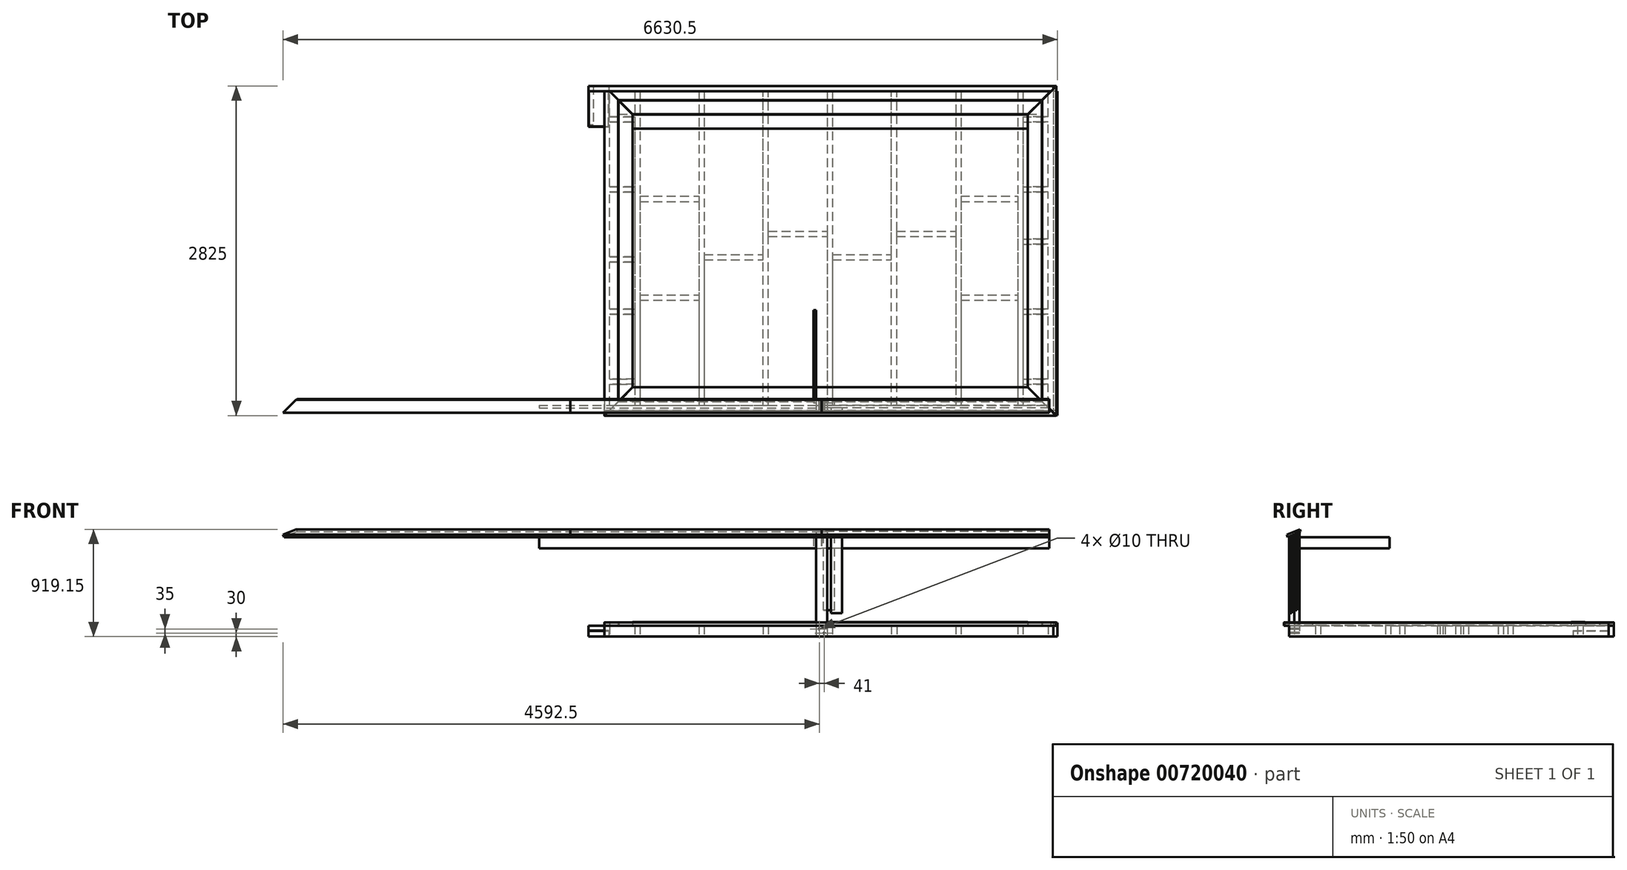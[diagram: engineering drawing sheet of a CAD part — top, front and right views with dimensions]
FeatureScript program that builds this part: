
annotation { "Feature Type Name" : "Feature", "Feature Type Description" : "" }
export const myFeature = defineFeature(function(context is Context, id is Id, definition is map)
    precondition{}
    {
        {
            var Q0;
            Q0=qCreatedBy(makeId("Top.planeOp"),FACE);
            var sketch = newSketch(context, id + "F0", { "sketchPlane" : qUnion([Q0])});
            skLineSegment(sketch, "E0.bottom", {"start": v(0, 0) * mm, "end": v(3980, 0) * mm});
            skLineSegment(sketch, "E0.top", {"start": v(0, -45) * mm, "end": v(3980, -45) * mm});
            skLineSegment(sketch, "E0.left", {"start": v(0, 0) * mm, "end": v(0, -45) * mm});
            skLineSegment(sketch, "E0.right", {"start": v(3980, 0) * mm, "end": v(3980, -45) * mm});
            skLineSegment(sketch, "E1.bottom", {"start": v(135, -2737) * mm, "end": v(3980, -2737) * mm});
            skLineSegment(sketch, "E1.top", {"start": v(135, -2782) * mm, "end": v(3980, -2782) * mm});
            skLineSegment(sketch, "E1.left", {"start": v(135, -2737) * mm, "end": v(135, -2782) * mm});
            skLineSegment(sketch, "E1.right", {"start": v(3980, -2737) * mm, "end": v(3980, -2782) * mm});
            skSolve(sketch);
        }
        {
            var Q0;
            Q0=makeQuery(id+"F0.imprint","IMPRINT",FACE,{"disambiguationData":[TD([[makeQuery(id+"F0.imprint","IMPRINT",EDGE,{"derivedFrom":sQuery(id+"F0.wireOp",EDGE,"E0.bottom")}),-1.0]])]});
            var Q1;
            Q1=makeQuery(id+"F0.imprint","IMPRINT",FACE,{"disambiguationData":[TD([[makeQuery(id+"F0.imprint","IMPRINT",EDGE,{"derivedFrom":sQuery(id+"F0.wireOp",EDGE,"E1.bottom")}),-1.0]])]});
            extrude(context, id + "F1", {"entities" : qUnion([Q0, Q1]), "depth" : 94 * mm, "offsetDistance" : 25 * mm});
        }
        {
            var Q0;
            Q0=qCreatedBy(makeId("Top.planeOp"),FACE);
            var sketch = newSketch(context, id + "F2", { "sketchPlane" : qUnion([Q0])});
            skLineSegment(sketch, "E2.bottom", {"start": v(945, -45) * mm, "end": v(990, -45) * mm});
            skLineSegment(sketch, "E2.top", {"start": v(945, -2737) * mm, "end": v(990, -2737) * mm});
            skLineSegment(sketch, "E2.left", {"start": v(945, -45) * mm, "end": v(945, -2737) * mm});
            skLineSegment(sketch, "E2.right", {"start": v(990, -45) * mm, "end": v(990, -2737) * mm});
            skLineSegment(sketch, "E3.bottom", {"start": v(1495, -2737) * mm, "end": v(1540, -2737) * mm});
            skLineSegment(sketch, "E3.top", {"start": v(1495, -45) * mm, "end": v(1540, -45) * mm});
            skLineSegment(sketch, "E3.left", {"start": v(1495, -2737) * mm, "end": v(1495, -45) * mm});
            skLineSegment(sketch, "E3.right", {"start": v(1540, -2737) * mm, "end": v(1540, -45) * mm});
            skLineSegment(sketch, "E4.bottom", {"start": v(2045, -45) * mm, "end": v(2090, -45) * mm});
            skLineSegment(sketch, "E4.top", {"start": v(2045, -2737) * mm, "end": v(2090, -2737) * mm});
            skLineSegment(sketch, "E4.left", {"start": v(2045, -45) * mm, "end": v(2045, -2737) * mm});
            skLineSegment(sketch, "E4.right", {"start": v(2090, -45) * mm, "end": v(2090, -2737) * mm});
            skLineSegment(sketch, "E5.bottom", {"start": v(2595, -2737) * mm, "end": v(2640, -2737) * mm});
            skLineSegment(sketch, "E5.top", {"start": v(2595, -45) * mm, "end": v(2640, -45) * mm});
            skLineSegment(sketch, "E5.left", {"start": v(2595, -2737) * mm, "end": v(2595, -45) * mm});
            skLineSegment(sketch, "E5.right", {"start": v(2640, -2737) * mm, "end": v(2640, -45) * mm});
            skLineSegment(sketch, "E6.bottom", {"start": v(3145, -45) * mm, "end": v(3190, -45) * mm});
            skLineSegment(sketch, "E6.top", {"start": v(3145, -2737) * mm, "end": v(3190, -2737) * mm});
            skLineSegment(sketch, "E6.left", {"start": v(3145, -45) * mm, "end": v(3145, -2737) * mm});
            skLineSegment(sketch, "E6.right", {"start": v(3190, -45) * mm, "end": v(3190, -2737) * mm});
            skLineSegment(sketch, "E7.bottom", {"start": v(3935, -2737) * mm, "end": v(3980, -2737) * mm});
            skLineSegment(sketch, "E7.top", {"start": v(3935, -45) * mm, "end": v(3980, -45) * mm});
            skLineSegment(sketch, "E7.left", {"start": v(3935, -2737) * mm, "end": v(3935, -45) * mm});
            skLineSegment(sketch, "E7.right", {"start": v(3980, -2737) * mm, "end": v(3980, -45) * mm});
            skLineSegment(sketch, "E8.bottom", {"start": v(395, -45) * mm, "end": v(440, -45) * mm});
            skLineSegment(sketch, "E8.top", {"start": v(395, -2737) * mm, "end": v(440, -2737) * mm});
            skLineSegment(sketch, "E8.left", {"start": v(395, -45) * mm, "end": v(395, -2737) * mm});
            skLineSegment(sketch, "E8.right", {"start": v(440, -45) * mm, "end": v(440, -2737) * mm});
            skLineSegment(sketch, "E9.bottom", {"start": v(3720, -45) * mm, "end": v(3675, -45) * mm});
            skLineSegment(sketch, "E9.top", {"start": v(3720, -2737) * mm, "end": v(3675, -2737) * mm});
            skLineSegment(sketch, "E9.left", {"start": v(3720, -45) * mm, "end": v(3720, -2737) * mm});
            skLineSegment(sketch, "E9.right", {"start": v(3675, -45) * mm, "end": v(3675, -2737) * mm});
            skLineSegment(sketch, "E10.0", {"start": v(0, -45) * mm, "end": v(3980, -45) * mm});
            skPoint(sketch, "E11.0", {"position": v(135, -2737) * mm});
            skLineSegment(sketch, "E12.bottom", {"start": v(135, -2737) * mm, "end": v(180, -2737) * mm});
            skLineSegment(sketch, "E12.top", {"start": v(135, -45) * mm, "end": v(180, -45) * mm});
            skLineSegment(sketch, "E12.left", {"start": v(135, -2737) * mm, "end": v(135, -45) * mm});
            skLineSegment(sketch, "E12.right", {"start": v(180, -2737) * mm, "end": v(180, -45) * mm});
            skSolve(sketch);
        }
        {
            var Q0;
            Q0=makeQuery(id+"F2.imprint","IMPRINT",FACE,{"disambiguationData":[TD([[makeQuery(id+"F2.imprint","IMPRINT",EDGE,{"derivedFrom":sQuery(id+"F2.wireOp",EDGE,"E12.bottom")}),1.0]])]});
            var Q1;
            Q1=makeQuery(id+"F2.imprint","IMPRINT",FACE,{"disambiguationData":[TD([[makeQuery(id+"F2.imprint","IMPRINT",EDGE,{"derivedFrom":sQuery(id+"F2.wireOp",EDGE,"E8.top")}),1.0]])]});
            var Q2;
            Q2=makeQuery(id+"F2.imprint","IMPRINT",FACE,{"disambiguationData":[TD([[makeQuery(id+"F2.imprint","IMPRINT",EDGE,{"derivedFrom":sQuery(id+"F2.wireOp",EDGE,"E2.top")}),1.0]])]});
            var Q3;
            Q3=makeQuery(id+"F2.imprint","IMPRINT",FACE,{"disambiguationData":[TD([[makeQuery(id+"F2.imprint","IMPRINT",EDGE,{"derivedFrom":sQuery(id+"F2.wireOp",EDGE,"E3.bottom")}),1.0]])]});
            var Q4;
            Q4=makeQuery(id+"F2.imprint","IMPRINT",FACE,{"disambiguationData":[TD([[makeQuery(id+"F2.imprint","IMPRINT",EDGE,{"derivedFrom":sQuery(id+"F2.wireOp",EDGE,"E4.top")}),1.0]])]});
            var Q5;
            Q5=makeQuery(id+"F2.imprint","IMPRINT",FACE,{"disambiguationData":[TD([[makeQuery(id+"F2.imprint","IMPRINT",EDGE,{"derivedFrom":sQuery(id+"F2.wireOp",EDGE,"E5.bottom")}),1.0]])]});
            var Q6;
            Q6=makeQuery(id+"F2.imprint","IMPRINT",FACE,{"disambiguationData":[TD([[makeQuery(id+"F2.imprint","IMPRINT",EDGE,{"derivedFrom":sQuery(id+"F2.wireOp",EDGE,"E6.top")}),1.0]])]});
            var Q7;
            Q7=makeQuery(id+"F2.imprint","IMPRINT",FACE,{"disambiguationData":[TD([[makeQuery(id+"F2.imprint","IMPRINT",EDGE,{"derivedFrom":sQuery(id+"F2.wireOp",EDGE,"E9.top")}),-1.0]])]});
            var Q8;
            Q8=makeQuery(id+"F2.imprint","IMPRINT",FACE,{"disambiguationData":[TD([[makeQuery(id+"F2.imprint","IMPRINT",EDGE,{"derivedFrom":sQuery(id+"F2.wireOp",EDGE,"E7.bottom")}),1.0]])]});
            extrude(context, id + "F3", {"entities" : qUnion([Q0, Q1, Q2, Q3, Q4, Q5, Q6, Q7, Q8]), "operationType" : NewBodyOperationType.ADD, "depth" : 95.5 * mm, "offsetDistance" : 25 * mm});
        }
        {
            var Q0;
            Q0=makeQuery(id+"F1.opExtrude","CAP_FACE",FACE,{"disambiguationData":[OSD([sQuery(id+"F0.wireOp",EDGE,"E0.bottom"),sQuery(id+"F0.wireOp",EDGE,"E0.top"),sQuery(id+"F0.wireOp",EDGE,"E0.left"),sQuery(id+"F0.wireOp",EDGE,"E0.right")])],"isStart":false});
            var sketch = newSketch(context, id + "F4", { "sketchPlane" : qUnion([Q0])});
            skLineSegment(sketch, "E13.bottom", {"start": v(135.7, 0) * mm, "end": v(4004.3, 0) * mm});
            skLineSegment(sketch, "E14.0", {"start": v(135.7, 0) * mm, "end": v(255.7, -120) * mm});
            skLineSegment(sketch, "E15.trimOffspring", {"start": v(255.7, -120) * mm, "end": v(3884.3, -120) * mm});
            skPoint(sketch, "E16.0", {"position": v(135, -2782) * mm});
            skLineSegment(sketch, "E17.left", {"start": v(135, -2824.3) * mm, "end": v(135, -0.7) * mm});
            skLineSegment(sketch, "E17.right", {"start": v(255, -2704.3) * mm, "end": v(255, -120.7) * mm});
            skPoint(sketch, "E18.0", {"position": v(0, 0) * mm});
            skLineSegment(sketch, "E19", {"start": v(135, -0.7) * mm, "end": v(255, -120.7) * mm});
            skLineSegment(sketch, "E20", {"start": v(135, -2824.3) * mm, "end": v(255, -2704.3) * mm});
            skLineSegment(sketch, "E21.bottom", {"start": v(135.7, -2825) * mm, "end": v(4004.3, -2825) * mm});
            skLineSegment(sketch, "E21.top", {"start": v(255.7, -2705) * mm, "end": v(3884.3, -2705) * mm});
            skPoint(sketch, "E22.0", {"position": v(3980, -2782) * mm});
            skLineSegment(sketch, "E23", {"start": v(3884.3, -2705) * mm, "end": v(4004.3, -2825) * mm});
            skLineSegment(sketch, "E24", {"start": v(255.7, -2705) * mm, "end": v(135.7, -2825) * mm});
            skLineSegment(sketch, "E25.left", {"start": v(4005, -0.7) * mm, "end": v(4005, -2824.3) * mm});
            skLineSegment(sketch, "E25.right", {"start": v(3885, -120.7) * mm, "end": v(3885, -2704.3) * mm});
            skLineSegment(sketch, "E26", {"start": v(4005, -2824.3) * mm, "end": v(3885, -2704.3) * mm});
            skLineSegment(sketch, "E27", {"start": v(4005, -0.7) * mm, "end": v(3885, -120.7) * mm});
            skLineSegment(sketch, "E28", {"start": v(3884.3, -120) * mm, "end": v(4004.3, 0) * mm});
            skPoint(sketch, "E29.0", {"position": v(3980, 0) * mm});
            skLineSegment(sketch, "E30", {"start": v(4004.3, 0) * mm, "end": v(4005, -0.7) * mm, "construction": true});
            skLineSegment(sketch, "E31", {"start": v(135.7, 0) * mm, "end": v(135, -0.7) * mm, "construction": true});
            skLineSegment(sketch, "E32", {"start": v(135.7, -2825) * mm, "end": v(135, -2824.3) * mm, "construction": true});
            skLineSegment(sketch, "E33", {"start": v(3881.3, -123) * mm, "end": v(3761.3, -243) * mm});
            skLineSegment(sketch, "E34", {"start": v(3761.3, -243) * mm, "end": v(378.7, -243) * mm});
            skLineSegment(sketch, "E35", {"start": v(378.7, -243) * mm, "end": v(258.7, -123) * mm});
            skLineSegment(sketch, "E36", {"start": v(258.7, -123) * mm, "end": v(3881.3, -123) * mm});
            skLineSegment(sketch, "E37", {"start": v(258, -123.7) * mm, "end": v(258, -2701.3) * mm});
            skLineSegment(sketch, "E38", {"start": v(258, -2701.3) * mm, "end": v(378, -2581.3) * mm});
            skLineSegment(sketch, "E39", {"start": v(378, -2581.3) * mm, "end": v(378, -243.7) * mm});
            skLineSegment(sketch, "E40", {"start": v(378, -243.7) * mm, "end": v(258, -123.7) * mm});
            skLineSegment(sketch, "E41", {"start": v(3762, -243.7) * mm, "end": v(3882, -123.7) * mm});
            skLineSegment(sketch, "E42", {"start": v(3882, -123.7) * mm, "end": v(3882, -2701.3) * mm});
            skLineSegment(sketch, "E43", {"start": v(3882, -2701.3) * mm, "end": v(3762, -2581.3) * mm});
            skLineSegment(sketch, "E44", {"start": v(3762, -2581.3) * mm, "end": v(3762, -243.7) * mm});
            skLineSegment(sketch, "E45", {"start": v(3761.3, -2582) * mm, "end": v(3881.3, -2702) * mm});
            skLineSegment(sketch, "E46", {"start": v(3881.3, -2702) * mm, "end": v(258.7, -2702) * mm});
            skLineSegment(sketch, "E47", {"start": v(258.7, -2702) * mm, "end": v(378.7, -2582) * mm});
            skLineSegment(sketch, "E48", {"start": v(378.7, -2582) * mm, "end": v(3761.3, -2582) * mm});
            skLineSegment(sketch, "E49", {"start": v(4005, -2824.3) * mm, "end": v(4004.3, -2825) * mm});
            skSolve(sketch);
        }
        {
            var Q0;
            {var subQ0=sQuery(id+"F4.wireOp",EDGE,"E15.trimOffspring");Q0=makeQuery(id+"F4.imprint","IMPRINT",FACE,{"disambiguationData":[TD([[makeQuery(id+"F4.imprint","IMPRINT",EDGE,{"derivedFrom":subQ0}),1.0]])]});}
            var Q1;
            {var subQ0=sQuery(id+"F4.wireOp",EDGE,"E13.bottom");Q1=makeQuery(id+"F4.imprint","IMPRINT",FACE,{"disambiguationData":[TD([[makeQuery(id+"F4.imprint","IMPRINT",EDGE,{"derivedFrom":subQ0}),-1.0]])]});}
            var Q2;
            {var subQ1=sQuery(id+"F4.wireOp",EDGE,"E17.right");Q2=makeQuery(id+"F4.imprint","IMPRINT",FACE,{"disambiguationData":[TD([[makeQuery(id+"F4.imprint","IMPRINT",EDGE,{"derivedFrom":subQ1}),1.0]])]});}
            var Q3;
            {var subQ0=sQuery(id+"F4.wireOp",EDGE,"E17.left");var subQ1=makeQuery(id+"F1.opExtrude","CAP_EDGE",EDGE,{"disambiguationData":[OSD([sQuery(id+"F0.wireOp",EDGE,"E0.top")])],"isStart":false});var subQ2=makeQuery(id+"F4.imprint","INTERSECT",VERTEX,{"derivedFrom":[subQ1,subQ0]});Q3=makeQuery(id+"F4.imprint","IMPRINT",FACE,{"disambiguationData":[TD([[makeQuery(id+"F4.imprint","IMPRINT",EDGE,{"disambiguationData":[TD([[subQ2,-1.0]])],"derivedFrom":subQ1}),1.0]])]});}
            var Q4;
            Q4=makeQuery(id+"F4.imprint","IMPRINT",FACE,{"disambiguationData":[TD([[makeQuery(id+"F4.imprint","IMPRINT",EDGE,{"derivedFrom":sQuery(id+"F4.wireOp",EDGE,"E21.top")}),-1.0]])]});
            var Q5;
            {var subQ1=sQuery(id+"F4.wireOp",EDGE,"E25.right");Q5=makeQuery(id+"F4.imprint","IMPRINT",FACE,{"disambiguationData":[TD([[makeQuery(id+"F4.imprint","IMPRINT",EDGE,{"derivedFrom":subQ1}),1.0]])]});}
            var Q6;
            Q6=makeQuery(id+"F4.imprint","IMPRINT",FACE,{"disambiguationData":[TD([[makeQuery(id+"F4.imprint","IMPRINT",EDGE,{"derivedFrom":sQuery(id+"F4.wireOp",EDGE,"E33")}),-1.0]])]});
            var Q7;
            Q7=makeQuery(id+"F4.imprint","IMPRINT",FACE,{"disambiguationData":[TD([[makeQuery(id+"F4.imprint","IMPRINT",EDGE,{"derivedFrom":sQuery(id+"F4.wireOp",EDGE,"E37")}),1.0]])]});
            var Q8;
            Q8=makeQuery(id+"F4.imprint","IMPRINT",FACE,{"disambiguationData":[TD([[makeQuery(id+"F4.imprint","IMPRINT",EDGE,{"derivedFrom":sQuery(id+"F4.wireOp",EDGE,"E41")}),-1.0]])]});
            var Q9;
            Q9=makeQuery(id+"F4.imprint","IMPRINT",FACE,{"disambiguationData":[TD([[makeQuery(id+"F4.imprint","IMPRINT",EDGE,{"derivedFrom":sQuery(id+"F4.wireOp",EDGE,"E45")}),-1.0]])]});
            var Q10;
            {var subQ3=sQuery(id+"F4.wireOp",EDGE,"E28");var subQ5=makeQuery(id+"F1.opExtrude","CAP_EDGE",EDGE,{"disambiguationData":[OSD([sQuery(id+"F0.wireOp",EDGE,"E0.top")])],"isStart":false});var subQ6=makeQuery(id+"F4.imprint","INTERSECT",VERTEX,{"derivedFrom":[subQ5,subQ3]});Q10=makeQuery(id+"F4.imprint","IMPRINT",FACE,{"disambiguationData":[TD([[makeQuery(id+"F4.imprint","IMPRINT",EDGE,{"disambiguationData":[TD([[subQ6,-1.0]])],"derivedFrom":subQ3}),1.0]])]});}
            var Q11;
            {var subQ0=sQuery(id+"F4.wireOp",EDGE,"E27");var subQ1=makeQuery(id+"F1.opExtrude","CAP_EDGE",EDGE,{"disambiguationData":[OSD([sQuery(id+"F0.wireOp",EDGE,"E0.right")])],"isStart":false});var subQ2=makeQuery(id+"F4.imprint","INTERSECT",VERTEX,{"derivedFrom":[subQ1,subQ0]});Q11=makeQuery(id+"F4.imprint","IMPRINT",FACE,{"disambiguationData":[TD([[makeQuery(id+"F4.imprint","IMPRINT",EDGE,{"disambiguationData":[TD([[subQ2,-1.0]])],"derivedFrom":subQ0}),1.0]])]});}
            extrude(context, id + "F5", {"entities" : qUnion([Q0, Q1, Q2, Q3, Q4, Q5, Q6, Q7, Q8, Q9, Q10, Q11]), "depth" : 28 * mm, "offsetDistance" : 25 * mm});
        }
        {
            var Q0;
            Q0=qCreatedBy(makeId("Top.planeOp"),FACE);
            var sketch = newSketch(context, id + "F6", { "sketchPlane" : qUnion([Q0])});
            skLineSegment(sketch, "E50.0", {"start": v(945, -45) * mm, "end": v(945, -2737) * mm});
            skLineSegment(sketch, "E51.bottom", {"start": v(440, -1792) * mm, "end": v(945, -1792) * mm});
            skLineSegment(sketch, "E51.top", {"start": v(440, -1837) * mm, "end": v(945, -1837) * mm});
            skLineSegment(sketch, "E51.left", {"start": v(440, -1792) * mm, "end": v(440, -1837) * mm});
            skLineSegment(sketch, "E51.right", {"start": v(945, -1792) * mm, "end": v(945, -1837) * mm});
            skLineSegment(sketch, "E52.0", {"start": v(990, -45) * mm, "end": v(990, -2737) * mm});
            skLineSegment(sketch, "E53.0", {"start": v(1495, -2737) * mm, "end": v(1495, -45) * mm});
            skLineSegment(sketch, "E54.bottom", {"start": v(990, -1445) * mm, "end": v(1495, -1445) * mm});
            skLineSegment(sketch, "E54.top", {"start": v(990, -1490) * mm, "end": v(1495, -1490) * mm});
            skLineSegment(sketch, "E54.left", {"start": v(990, -1445) * mm, "end": v(990, -1490) * mm});
            skLineSegment(sketch, "E54.right", {"start": v(1495, -1445) * mm, "end": v(1495, -1490) * mm});
            skLineSegment(sketch, "E55.0", {"start": v(1540, -2737) * mm, "end": v(1540, -45) * mm});
            skLineSegment(sketch, "E56.0", {"start": v(2045, -45) * mm, "end": v(2045, -2737) * mm});
            skLineSegment(sketch, "E57.0", {"start": v(2090, -45) * mm, "end": v(2090, -2737) * mm});
            skLineSegment(sketch, "E58.0", {"start": v(2595, -2737) * mm, "end": v(2595, -45) * mm});
            skLineSegment(sketch, "E59.0", {"start": v(2640, -2737) * mm, "end": v(2640, -45) * mm});
            skLineSegment(sketch, "E60.0", {"start": v(3145, -45) * mm, "end": v(3145, -2737) * mm});
            skLineSegment(sketch, "E61.0", {"start": v(3190, -45) * mm, "end": v(3190, -2737) * mm});
            skLineSegment(sketch, "E62.0", {"start": v(3935, -2737) * mm, "end": v(3935, -45) * mm});
            skLineSegment(sketch, "E63.bottom", {"start": v(1540, -1290) * mm, "end": v(2045, -1290) * mm});
            skLineSegment(sketch, "E63.top", {"start": v(1540, -1245) * mm, "end": v(2045, -1245) * mm});
            skLineSegment(sketch, "E63.left", {"start": v(1540, -1290) * mm, "end": v(1540, -1245) * mm});
            skLineSegment(sketch, "E63.right", {"start": v(2045, -1290) * mm, "end": v(2045, -1245) * mm});
            skLineSegment(sketch, "E64.bottom", {"start": v(2090, -1445) * mm, "end": v(2595, -1445) * mm});
            skLineSegment(sketch, "E64.top", {"start": v(2090, -1490) * mm, "end": v(2595, -1490) * mm});
            skLineSegment(sketch, "E64.left", {"start": v(2090, -1445) * mm, "end": v(2090, -1490) * mm});
            skLineSegment(sketch, "E64.right", {"start": v(2595, -1445) * mm, "end": v(2595, -1490) * mm});
            skLineSegment(sketch, "E65.bottom", {"start": v(2640, -1290) * mm, "end": v(3145, -1290) * mm});
            skLineSegment(sketch, "E65.top", {"start": v(2640, -1245) * mm, "end": v(3145, -1245) * mm});
            skLineSegment(sketch, "E65.left", {"start": v(2640, -1290) * mm, "end": v(2640, -1245) * mm});
            skLineSegment(sketch, "E65.right", {"start": v(3145, -1290) * mm, "end": v(3145, -1245) * mm});
            skLineSegment(sketch, "E66.bottom", {"start": v(3190, -945) * mm, "end": v(3675, -945) * mm});
            skLineSegment(sketch, "E66.top", {"start": v(3190, -990) * mm, "end": v(3675, -990) * mm});
            skLineSegment(sketch, "E66.left", {"start": v(3190, -945) * mm, "end": v(3190, -990) * mm});
            skLineSegment(sketch, "E66.right", {"start": v(3675, -945) * mm, "end": v(3675, -990) * mm});
            skLineSegment(sketch, "E67.bottom", {"start": v(3190, -1792) * mm, "end": v(3675, -1792) * mm});
            skLineSegment(sketch, "E67.top", {"start": v(3190, -1837) * mm, "end": v(3675, -1837) * mm});
            skLineSegment(sketch, "E67.left", {"start": v(3190, -1792) * mm, "end": v(3190, -1837) * mm});
            skLineSegment(sketch, "E67.right", {"start": v(3675, -1792) * mm, "end": v(3675, -1837) * mm});
            skLineSegment(sketch, "E68.0", {"start": v(440, -45) * mm, "end": v(440, -2737) * mm});
            skLineSegment(sketch, "E69.bottom", {"start": v(440, -990) * mm, "end": v(945, -990) * mm});
            skLineSegment(sketch, "E69.top", {"start": v(440, -945) * mm, "end": v(945, -945) * mm});
            skLineSegment(sketch, "E69.left", {"start": v(440, -990) * mm, "end": v(440, -945) * mm});
            skLineSegment(sketch, "E69.right", {"start": v(945, -990) * mm, "end": v(945, -945) * mm});
            skLineSegment(sketch, "E70.0", {"start": v(395, -45) * mm, "end": v(395, -2737) * mm});
            skLineSegment(sketch, "E71.0", {"start": v(180, -2737) * mm, "end": v(180, -45) * mm});
            skLineSegment(sketch, "E72.bottom", {"start": v(180, -310) * mm, "end": v(395, -310) * mm});
            skLineSegment(sketch, "E72.top", {"start": v(180, -265) * mm, "end": v(395, -265) * mm});
            skLineSegment(sketch, "E72.left", {"start": v(180, -310) * mm, "end": v(180, -265) * mm});
            skLineSegment(sketch, "E72.right", {"start": v(395, -310) * mm, "end": v(395, -265) * mm});
            skLineSegment(sketch, "E73.bottom", {"start": v(395, -2557) * mm, "end": v(180, -2557) * mm});
            skLineSegment(sketch, "E73.top", {"start": v(395, -2512) * mm, "end": v(180, -2512) * mm});
            skLineSegment(sketch, "E73.left", {"start": v(395, -2557) * mm, "end": v(395, -2512) * mm});
            skLineSegment(sketch, "E73.right", {"start": v(180, -2557) * mm, "end": v(180, -2512) * mm});
            skLineSegment(sketch, "E74.bottom", {"start": v(180, -1957) * mm, "end": v(395, -1957) * mm});
            skLineSegment(sketch, "E74.top", {"start": v(180, -1912) * mm, "end": v(395, -1912) * mm});
            skLineSegment(sketch, "E74.left", {"start": v(180, -1957) * mm, "end": v(180, -1912) * mm});
            skLineSegment(sketch, "E74.right", {"start": v(395, -1957) * mm, "end": v(395, -1912) * mm});
            skLineSegment(sketch, "E75.bottom", {"start": v(180, -1510) * mm, "end": v(395, -1510) * mm});
            skLineSegment(sketch, "E75.top", {"start": v(180, -1465) * mm, "end": v(395, -1465) * mm});
            skLineSegment(sketch, "E75.left", {"start": v(180, -1510) * mm, "end": v(180, -1465) * mm});
            skLineSegment(sketch, "E75.right", {"start": v(395, -1510) * mm, "end": v(395, -1465) * mm});
            skLineSegment(sketch, "E76.bottom", {"start": v(180, -910) * mm, "end": v(395, -910) * mm});
            skLineSegment(sketch, "E76.top", {"start": v(180, -865) * mm, "end": v(395, -865) * mm});
            skLineSegment(sketch, "E76.left", {"start": v(180, -910) * mm, "end": v(180, -865) * mm});
            skLineSegment(sketch, "E76.right", {"start": v(395, -910) * mm, "end": v(395, -865) * mm});
            skLineSegment(sketch, "E77.0", {"start": v(3720, -45) * mm, "end": v(3720, -2737) * mm});
            skLineSegment(sketch, "E78.bottom", {"start": v(3720, -2557) * mm, "end": v(3935, -2557) * mm});
            skLineSegment(sketch, "E78.top", {"start": v(3720, -2512) * mm, "end": v(3935, -2512) * mm});
            skLineSegment(sketch, "E78.left", {"start": v(3720, -2557) * mm, "end": v(3720, -2512) * mm});
            skLineSegment(sketch, "E78.right", {"start": v(3935, -2557) * mm, "end": v(3935, -2512) * mm});
            skLineSegment(sketch, "E79.bottom", {"start": v(3720, -1957) * mm, "end": v(3935, -1957) * mm});
            skLineSegment(sketch, "E79.top", {"start": v(3720, -1912) * mm, "end": v(3935, -1912) * mm});
            skLineSegment(sketch, "E79.left", {"start": v(3720, -1957) * mm, "end": v(3720, -1912) * mm});
            skLineSegment(sketch, "E79.right", {"start": v(3935, -1957) * mm, "end": v(3935, -1912) * mm});
            skLineSegment(sketch, "E80.bottom", {"start": v(3720, -1357) * mm, "end": v(3935, -1357) * mm});
            skLineSegment(sketch, "E80.top", {"start": v(3720, -1312) * mm, "end": v(3935, -1312) * mm});
            skLineSegment(sketch, "E80.left", {"start": v(3720, -1357) * mm, "end": v(3720, -1312) * mm});
            skLineSegment(sketch, "E80.right", {"start": v(3935, -1357) * mm, "end": v(3935, -1312) * mm});
            skLineSegment(sketch, "E81.bottom", {"start": v(3720, -265) * mm, "end": v(3935, -265) * mm});
            skLineSegment(sketch, "E81.top", {"start": v(3720, -310) * mm, "end": v(3935, -310) * mm});
            skLineSegment(sketch, "E81.left", {"start": v(3720, -265) * mm, "end": v(3720, -310) * mm});
            skLineSegment(sketch, "E81.right", {"start": v(3935, -265) * mm, "end": v(3935, -310) * mm});
            skLineSegment(sketch, "E82.bottom", {"start": v(3720, -910) * mm, "end": v(3935, -910) * mm});
            skLineSegment(sketch, "E82.top", {"start": v(3720, -865) * mm, "end": v(3935, -865) * mm});
            skLineSegment(sketch, "E82.left", {"start": v(3720, -910) * mm, "end": v(3720, -865) * mm});
            skLineSegment(sketch, "E82.right", {"start": v(3935, -910) * mm, "end": v(3935, -865) * mm});
            skSolve(sketch);
        }
        {
            var Q0;
            Q0=makeQuery(id+"F6.imprint","IMPRINT",FACE,{"disambiguationData":[TD([[makeQuery(id+"F6.imprint","IMPRINT",EDGE,{"derivedFrom":sQuery(id+"F6.wireOp",EDGE,"E72.bottom")}),1.0]])]});
            var Q1;
            Q1=makeQuery(id+"F6.imprint","IMPRINT",FACE,{"disambiguationData":[TD([[makeQuery(id+"F6.imprint","IMPRINT",EDGE,{"derivedFrom":sQuery(id+"F6.wireOp",EDGE,"E76.bottom")}),1.0]])]});
            var Q2;
            Q2=makeQuery(id+"F6.imprint","IMPRINT",FACE,{"disambiguationData":[TD([[makeQuery(id+"F6.imprint","IMPRINT",EDGE,{"derivedFrom":sQuery(id+"F6.wireOp",EDGE,"E75.bottom")}),1.0]])]});
            var Q3;
            Q3=makeQuery(id+"F6.imprint","IMPRINT",FACE,{"disambiguationData":[TD([[makeQuery(id+"F6.imprint","IMPRINT",EDGE,{"derivedFrom":sQuery(id+"F6.wireOp",EDGE,"E69.bottom")}),1.0]])]});
            var Q4;
            {var subQ0=sQuery(id+"F6.wireOp",EDGE,"E51.bottom");Q4=makeQuery(id+"F6.imprint","IMPRINT",FACE,{"disambiguationData":[TD([[makeQuery(id+"F6.imprint","IMPRINT",EDGE,{"derivedFrom":subQ0}),-1.0]])]});}
            var Q5;
            Q5=makeQuery(id+"F6.imprint","IMPRINT",FACE,{"disambiguationData":[TD([[makeQuery(id+"F6.imprint","IMPRINT",EDGE,{"derivedFrom":sQuery(id+"F6.wireOp",EDGE,"E74.bottom")}),1.0]])]});
            var Q6;
            Q6=makeQuery(id+"F6.imprint","IMPRINT",FACE,{"disambiguationData":[TD([[makeQuery(id+"F6.imprint","IMPRINT",EDGE,{"derivedFrom":sQuery(id+"F6.wireOp",EDGE,"E73.bottom")}),-1.0]])]});
            var Q7;
            Q7=makeQuery(id+"F6.imprint","IMPRINT",FACE,{"disambiguationData":[TD([[makeQuery(id+"F6.imprint","IMPRINT",EDGE,{"derivedFrom":sQuery(id+"F6.wireOp",EDGE,"E54.bottom")}),-1.0]])]});
            var Q8;
            Q8=makeQuery(id+"F6.imprint","IMPRINT",FACE,{"disambiguationData":[TD([[makeQuery(id+"F6.imprint","IMPRINT",EDGE,{"derivedFrom":sQuery(id+"F6.wireOp",EDGE,"E63.bottom")}),1.0]])]});
            var Q9;
            Q9=makeQuery(id+"F6.imprint","IMPRINT",FACE,{"disambiguationData":[TD([[makeQuery(id+"F6.imprint","IMPRINT",EDGE,{"derivedFrom":sQuery(id+"F6.wireOp",EDGE,"E64.bottom")}),-1.0]])]});
            var Q10;
            Q10=makeQuery(id+"F6.imprint","IMPRINT",FACE,{"disambiguationData":[TD([[makeQuery(id+"F6.imprint","IMPRINT",EDGE,{"derivedFrom":sQuery(id+"F6.wireOp",EDGE,"E65.bottom")}),1.0]])]});
            var Q11;
            Q11=makeQuery(id+"F6.imprint","IMPRINT",FACE,{"disambiguationData":[TD([[makeQuery(id+"F6.imprint","IMPRINT",EDGE,{"derivedFrom":sQuery(id+"F6.wireOp",EDGE,"E66.bottom")}),-1.0]])]});
            var Q12;
            Q12=makeQuery(id+"F6.imprint","IMPRINT",FACE,{"disambiguationData":[TD([[makeQuery(id+"F6.imprint","IMPRINT",EDGE,{"derivedFrom":sQuery(id+"F6.wireOp",EDGE,"E67.bottom")}),-1.0]])]});
            var Q13;
            Q13=makeQuery(id+"F6.imprint","IMPRINT",FACE,{"disambiguationData":[TD([[makeQuery(id+"F6.imprint","IMPRINT",EDGE,{"derivedFrom":sQuery(id+"F6.wireOp",EDGE,"E78.bottom")}),1.0]])]});
            var Q14;
            Q14=makeQuery(id+"F6.imprint","IMPRINT",FACE,{"disambiguationData":[TD([[makeQuery(id+"F6.imprint","IMPRINT",EDGE,{"derivedFrom":sQuery(id+"F6.wireOp",EDGE,"E79.bottom")}),1.0]])]});
            var Q15;
            Q15=makeQuery(id+"F6.imprint","IMPRINT",FACE,{"disambiguationData":[TD([[makeQuery(id+"F6.imprint","IMPRINT",EDGE,{"derivedFrom":sQuery(id+"F6.wireOp",EDGE,"E80.bottom")}),1.0]])]});
            var Q16;
            Q16=makeQuery(id+"F6.imprint","IMPRINT",FACE,{"disambiguationData":[TD([[makeQuery(id+"F6.imprint","IMPRINT",EDGE,{"derivedFrom":sQuery(id+"F6.wireOp",EDGE,"E82.bottom")}),1.0]])]});
            var Q17;
            Q17=makeQuery(id+"F6.imprint","IMPRINT",FACE,{"disambiguationData":[TD([[makeQuery(id+"F6.imprint","IMPRINT",EDGE,{"derivedFrom":sQuery(id+"F6.wireOp",EDGE,"E81.bottom")}),-1.0]])]});
            extrude(context, id + "F7", {"entities" : qUnion([Q0, Q1, Q2, Q3, Q4, Q5, Q6, Q7, Q8, Q9, Q10, Q11, Q12, Q13, Q14, Q15, Q16, Q17]), "operationType" : NewBodyOperationType.ADD, "depth" : 95 * mm, "offsetDistance" : 25 * mm});
        }
        {
            var Q0;
            Q0=qCreatedBy(makeId("Top.planeOp"),FACE);
            var sketch = newSketch(context, id + "F8", { "sketchPlane" : qUnion([Q0])});
            skPoint(sketch, "E83.0", {"position": v(2045, -2737) * mm});
            skLineSegment(sketch, "E84.bottom", {"start": v(2045, -2737) * mm, "end": v(1950, -2737) * mm});
            skLineSegment(sketch, "E84.top", {"start": v(2045, -2692) * mm, "end": v(1950, -2692) * mm});
            skLineSegment(sketch, "E84.left", {"start": v(2045, -2737) * mm, "end": v(2045, -2692) * mm});
            skLineSegment(sketch, "E84.right", {"start": v(1950, -2737) * mm, "end": v(1950, -2692) * mm});
            skSolve(sketch);
        }
        {
            var Q0;
            Q0=makeQuery(id+"F8.imprint","IMPRINT",FACE,{"disambiguationData":[TD([[makeQuery(id+"F8.imprint","IMPRINT",EDGE,{"derivedFrom":sQuery(id+"F8.wireOp",EDGE,"E84.bottom")}),-1.0]])]});
            extrude(context, id + "F9", {"entities" : qUnion([Q0]), "depth" : 895 * mm, "offsetDistance" : 25 * mm});
        }
        {
            var Q0;
            Q0=makeQuery(id+"F9.opExtrude","SWEPT_EDGE",EDGE,{"disambiguationData":[OSD([sQuery(id+"F8.wireOp",EDGE,"E84.bottom"),sQuery(id+"F8.wireOp",EDGE,"E84.right")])]});
            var Q1;
            Q1=makeQuery(id+"F9.opExtrude","SWEPT_EDGE",EDGE,{"disambiguationData":[OSD([sQuery(id+"F8.wireOp",EDGE,"E84.bottom"),sQuery(id+"F8.wireOp",EDGE,"E84.left")])]});
            var Q2;
            Q2=makeQuery(id+"F9.opExtrude","SWEPT_EDGE",EDGE,{"disambiguationData":[OSD([sQuery(id+"F8.wireOp",EDGE,"E84.top"),sQuery(id+"F8.wireOp",EDGE,"E84.left")])]});
            var Q3;
            Q3=makeQuery(id+"F9.opExtrude","SWEPT_EDGE",EDGE,{"disambiguationData":[OSD([sQuery(id+"F8.wireOp",EDGE,"E84.top"),sQuery(id+"F8.wireOp",EDGE,"E84.right")])]});
            fillet(context, id + "F10", {"entities" : qUnion([Q0, Q1, Q2, Q3]), "radius" : 2 * mm, "tangentPropagation" : true, "allowEdgeOverflow" : false});
        }
        {
            var Q0;
            Q0=makeQuery(id+"F9.opExtrude","CAP_FACE",FACE,{"disambiguationData":[OSD([sQuery(id+"F8.wireOp",EDGE,"E84.bottom"),sQuery(id+"F8.wireOp",EDGE,"E84.top"),sQuery(id+"F8.wireOp",EDGE,"E84.left"),sQuery(id+"F8.wireOp",EDGE,"E84.right")])],"isStart":true});
            var sketch = newSketch(context, id + "F11", { "sketchPlane" : qUnion([Q0])});
            skLineSegment(sketch, "E85.bottom", {"start": v(2045, 2782) * mm, "end": v(1950, 2782) * mm});
            skLineSegment(sketch, "E85.top", {"start": v(2045, 2737) * mm, "end": v(1950, 2737) * mm});
            skLineSegment(sketch, "E85.left", {"start": v(2045, 2782) * mm, "end": v(2045, 2737) * mm});
            skLineSegment(sketch, "E85.right", {"start": v(1950, 2782) * mm, "end": v(1950, 2737) * mm});
            skSolve(sketch);
        }
        {
            var Q0;
            Q0 = qSketchRegion(id + "F11", true);
            extrude(context, id + "F12", {"entities" : qUnion([Q0]), "oppositeDirection" : true, "depth" : 895 * mm, "offsetDistance" : 25 * mm, "hasSecondDirection" : true, "secondDirectionOppositeDirection" : true, "secondDirectionDepth" : 95 * mm});
        }
        {
            var Q0;
            Q0=makeQuery(id+"F12.opExtrude","SWEPT_EDGE",EDGE,{"disambiguationData":[OSD([sQuery(id+"F11.wireOp",EDGE,"E85.bottom"),sQuery(id+"F11.wireOp",EDGE,"E85.right")])]});
            var Q1;
            Q1=makeQuery(id+"F12.opExtrude","SWEPT_EDGE",EDGE,{"disambiguationData":[OSD([sQuery(id+"F11.wireOp",EDGE,"E85.bottom"),sQuery(id+"F11.wireOp",EDGE,"E85.left")])]});
            var Q2;
            Q2=makeQuery(id+"F12.opExtrude","SWEPT_EDGE",EDGE,{"disambiguationData":[OSD([sQuery(id+"F11.wireOp",EDGE,"E85.top"),sQuery(id+"F11.wireOp",EDGE,"E85.right")])]});
            var Q3;
            Q3=makeQuery(id+"F12.opExtrude","SWEPT_EDGE",EDGE,{"disambiguationData":[OSD([sQuery(id+"F11.wireOp",EDGE,"E85.top"),sQuery(id+"F11.wireOp",EDGE,"E85.left")])]});
            fillet(context, id + "F13", {"entities" : qUnion([Q0, Q1, Q2, Q3]), "radius" : 2 * mm, "tangentPropagation" : true, "allowEdgeOverflow" : false});
        }
        {
            var Q0;
            Q0=makeQuery(id+"F1.opExtrude","SWEPT_FACE",FACE,{"disambiguationData":[OSD([sQuery(id+"F0.wireOp",EDGE,"E1.top")])]});
            var sketch = newSketch(context, id + "F14", { "sketchPlane" : qUnion([Q0])});
            skLineSegment(sketch, "E86.0.0", {"start": v(1952, 95) * mm, "end": v(2043, 95) * mm});
            skLineSegment(sketch, "E86.0.1", {"start": v(2043, 95) * mm, "end": v(2043, 895) * mm});
            skLineSegment(sketch, "E86.0.2", {"start": v(2043, 895) * mm, "end": v(1952, 895) * mm});
            skLineSegment(sketch, "E86.0.3", {"start": v(1952, 895) * mm, "end": v(1952, 95) * mm});
            skCircle(sketch, "E87", {"center": v(1977, 65) * mm, "radius": 5 * mm});
            skCircle(sketch, "E88", {"center": v(2018, 30) * mm, "radius": 5 * mm});
            skSolve(sketch);
        }
        {
            var Q0;
            Q0=makeQuery(id+"F14.imprint","IMPRINT",FACE,{"disambiguationData":[TD([[makeQuery(id+"F14.imprint","IMPRINT",EDGE,{"derivedFrom":sQuery(id+"F14.wireOp",EDGE,"E87")}),1.0]])]});
            var Q1;
            Q1=makeQuery(id+"F14.imprint","IMPRINT",FACE,{"disambiguationData":[TD([[makeQuery(id+"F14.imprint","IMPRINT",EDGE,{"derivedFrom":sQuery(id+"F14.wireOp",EDGE,"E88")}),1.0]])]});
            extrude(context, id + "F15", {"entities" : qUnion([Q0, Q1]), "operationType" : NewBodyOperationType.REMOVE, "oppositeDirection" : true, "depth" : 150 * mm, "offsetDistance" : 25 * mm});
        }
        {
            var Q0;
            Q0=makeQuery(id+"F9.opExtrude","SWEPT_FACE",FACE,{"disambiguationData":[OSD([sQuery(id+"F8.wireOp",EDGE,"E84.right")])]});
            var sketch = newSketch(context, id + "F16", { "sketchPlane" : qUnion([Q0])});
            skPoint(sketch, "E89.0", {"position": v(2692, 895) * mm});
            skLineSegment(sketch, "E90", {"start": v(2592, 936.42) * mm, "end": v(2792, 853.58) * mm});
            skLineSegment(sketch, "E91", {"start": v(2592, 936.42) * mm, "end": v(2792, 936.42) * mm});
            skLineSegment(sketch, "E92", {"start": v(2792, 936.42) * mm, "end": v(2792, 853.58) * mm});
            skSolve(sketch);
        }
        {
            var Q0;
            Q0 = qSketchRegion(id + "F16", true);
            extrude(context, id + "F17", {"entities" : qUnion([Q0]), "operationType" : NewBodyOperationType.REMOVE, "oppositeDirection" : true, "depth" : 150 * mm, "offsetDistance" : 25 * mm, "hasSecondDirection" : true, "secondDirectionOppositeDirection" : false, "secondDirectionDepth" : 150 * mm});
        }
        {
            var Q0;
            Q0=makeQuery(id+"F12.opExtrude","SWEPT_FACE",FACE,{"disambiguationData":[OSD([sQuery(id+"F11.wireOp",EDGE,"E85.right")])]});
            var sketch = newSketch(context, id + "F18", { "sketchPlane" : qUnion([Q0])});
            skLineSegment(sketch, "E93.0", {"start": v(2694, 894.17) * mm, "end": v(2735, 877.19) * mm});
            skLineSegment(sketch, "E94", {"start": v(2735, 877.19) * mm, "end": v(2844, 832.04) * mm});
            skLineSegment(sketch, "E95", {"start": v(2844, 832.04) * mm, "end": v(2844, 935.6) * mm});
            skLineSegment(sketch, "E96", {"start": v(2844, 935.6) * mm, "end": v(2594, 935.6) * mm});
            skLineSegment(sketch, "E97", {"start": v(2594, 935.6) * mm, "end": v(2694, 894.17) * mm});
            skSolve(sketch);
        }
        {
            var Q0;
            Q0 = qSketchRegion(id + "F18", true);
            extrude(context, id + "F19", {"entities" : qUnion([Q0]), "operationType" : NewBodyOperationType.REMOVE, "oppositeDirection" : true, "depth" : 150 * mm, "offsetDistance" : 25 * mm, "hasSecondDirection" : true, "secondDirectionOppositeDirection" : false, "secondDirectionDepth" : 100 * mm});
        }
        {
            var Q0;
            Q0=makeQuery(id+"F9.opExtrude","SWEPT_FACE",FACE,{"disambiguationData":[OSD([sQuery(id+"F8.wireOp",EDGE,"E84.left")])]});
            var sketch = newSketch(context, id + "F20", { "sketchPlane" : qUnion([Q0])});
            skLineSegment(sketch, "E98.bottom", {"start": v(-2759, 850.36) * mm, "end": v(-2737, 850.36) * mm});
            skLineSegment(sketch, "E98.top", {"start": v(-2759, 755.36) * mm, "end": v(-2737, 755.36) * mm});
            skLineSegment(sketch, "E98.left", {"start": v(-2759, 850.36) * mm, "end": v(-2759, 755.36) * mm});
            skLineSegment(sketch, "E98.right", {"start": v(-2737, 850.36) * mm, "end": v(-2737, 755.36) * mm});
            skPoint(sketch, "E99.0", {"position": v(-2737, 876.36) * mm});
            skPoint(sketch, "E100.0", {"position": v(-2692, 895) * mm});
            skSolve(sketch);
        }
        {
            var Q0;
            Q0=makeQuery(id+"F20.imprint","IMPRINT",FACE,{"disambiguationData":[TD([[makeQuery(id+"F20.imprint","IMPRINT",EDGE,{"derivedFrom":sQuery(id+"F20.wireOp",EDGE,"E98.bottom")}),-1.0]])]});
            extrude(context, id + "F21", {"entities" : qUnion([Q0]), "depth" : 1900 * mm, "offsetDistance" : 25 * mm, "hasSecondDirection" : true, "secondDirectionOppositeDirection" : true, "secondDirectionDepth" : (95 / 2) * mm});
        }
        {
            var Q0;
            Q0=makeQuery(id+"F21.opExtrude","SWEPT_FACE",FACE,{"disambiguationData":[OSD([sQuery(id+"F20.wireOp",EDGE,"E98.bottom")])]});
            var sketch = newSketch(context, id + "F22", { "sketchPlane" : qUnion([Q0])});
            skPoint(sketch, "E101.0", {"position": v(1997.5, -2759) * mm});
            skLineSegment(sketch, "E102.bottom", {"start": v(2077, -2759) * mm, "end": v(2172, -2759) * mm});
            skLineSegment(sketch, "E102.top", {"start": v(2077, -2781) * mm, "end": v(2172, -2781) * mm});
            skLineSegment(sketch, "E102.left", {"start": v(2077, -2759) * mm, "end": v(2077, -2781) * mm});
            skLineSegment(sketch, "E102.right", {"start": v(2172, -2759) * mm, "end": v(2172, -2781) * mm});
            skSolve(sketch);
        }
        {
            var Q0;
            Q0 = qSketchRegion(id + "F22", true);
            extrude(context, id + "F23", {"entities" : qUnion([Q0]), "oppositeDirection" : true, "depth" : 650 * mm, "offsetDistance" : 25 * mm});
        }
        {
            var Q0;
            Q0=makeQuery(id+"F9.opExtrude","SWEPT_FACE",FACE,{"disambiguationData":[OSD([sQuery(id+"F8.wireOp",EDGE,"E84.left")])]});
            var sketch = newSketch(context, id + "F24", { "sketchPlane" : qUnion([Q0])});
            skPoint(sketch, "E103.0", {"position": v(-2692, 895) * mm});
            skPoint(sketch, "E104.0", {"position": v(-2737, 876.36) * mm});
            skLineSegment(sketch, "E105", {"start": v(-2682.76, 898.83) * mm, "end": v(-2793.63, 852.9) * mm});
            skLineSegment(sketch, "E106", {"start": v(-2793.63, 852.9) * mm, "end": v(-2802.05, 873.23) * mm});
            skLineSegment(sketch, "E107", {"start": v(-2802.05, 873.23) * mm, "end": v(-2691.18, 919.15) * mm});
            skLineSegment(sketch, "E108", {"start": v(-2691.18, 919.15) * mm, "end": v(-2682.76, 898.83) * mm});
            skSolve(sketch);
        }
        {
            var Q0;
            {var subQ0=sQuery(id+"F24.wireOp",EDGE,"E106");Q0=makeQuery(id+"F24.imprint","IMPRINT",FACE,{"disambiguationData":[TD([[makeQuery(id+"F24.imprint","IMPRINT",EDGE,{"derivedFrom":subQ0}),-1.0]])]});}
            extrude(context, id + "F25", {"entities" : qUnion([Q0]), "depth" : 1900 * mm, "offsetDistance" : 25 * mm, "hasSecondDirection" : true, "secondDirectionOppositeDirection" : true, "secondDirectionDepth" : (95 / 2) * mm});
        }
        {
            var Q0;
            Q0=makeQuery(id+"F21.opExtrude","SWEPT_FACE",FACE,{"disambiguationData":[OSD([sQuery(id+"F20.wireOp",EDGE,"E98.bottom")])]});
            var sketch = newSketch(context, id + "F26", { "sketchPlane" : qUnion([Q0])});
            skPoint(sketch, "E109.0", {"position": v(1997.5, -2737) * mm});
            skLineSegment(sketch, "E110.bottom", {"start": v(2012.5, -2737) * mm, "end": v(2107.5, -2737) * mm});
            skLineSegment(sketch, "E110.top", {"start": v(2012.5, -2715) * mm, "end": v(2107.5, -2715) * mm});
            skLineSegment(sketch, "E110.left", {"start": v(2012.5, -2737) * mm, "end": v(2012.5, -2715) * mm});
            skLineSegment(sketch, "E110.right", {"start": v(2107.5, -2737) * mm, "end": v(2107.5, -2715) * mm});
            skSolve(sketch);
        }
        {
            var Q0;
            Q0 = qSketchRegion(id + "F26", true);
            extrude(context, id + "F27", {"entities" : qUnion([Q0]), "oppositeDirection" : true, "depth" : 625 * mm, "offsetDistance" : 25 * mm, "hasSecondDirection" : true, "secondDirectionOppositeDirection" : false, "secondDirectionDepth" : 25 * mm});
        }
        {
            var Q0;
            Q0=qCreatedBy(makeId("Top.planeOp"),FACE);
            var sketch = newSketch(context, id + "F28", { "sketchPlane" : qUnion([Q0])});
            skLineSegment(sketch, "E111.bottom", {"start": v(0, 0) * mm, "end": v(175, 0) * mm});
            skLineSegment(sketch, "E111.top", {"start": v(0, -350) * mm, "end": v(175, -350) * mm});
            skLineSegment(sketch, "E111.left", {"start": v(0, 0) * mm, "end": v(0, -350) * mm});
            skLineSegment(sketch, "E111.right", {"start": v(175, 0) * mm, "end": v(175, -350) * mm});
            skSolve(sketch);
        }
        {
            var Q0;
            Q0 = qSketchRegion(id + "F28", true);
            extrude(context, id + "F29", {"entities" : qUnion([Q0]), "depth" : 50 * mm, "offsetDistance" : 25 * mm});
        }
        {
            var Q0;
            Q0=makeQuery(id+"F29.opExtrude","CAP_FACE",FACE,{"disambiguationData":[OSD([sQuery(id+"F28.wireOp",EDGE,"E111.bottom"),sQuery(id+"F28.wireOp",EDGE,"E111.top"),sQuery(id+"F28.wireOp",EDGE,"E111.left"),sQuery(id+"F28.wireOp",EDGE,"E111.right")])],"isStart":false});
            chamfer(context, id + "F30", {"entities" : qUnion([Q0]), "width" : 3 * mm, "tangentPropagation" : true});
        }
        {
            var Q0;
            Q0=qCreatedBy(makeId("Top.planeOp"),FACE);
            var sketch = newSketch(context, id + "F31", { "sketchPlane" : qUnion([Q0])});
            skLineSegment(sketch, "E112.bottom", {"start": v(0, 0) * mm, "end": v(40, 0) * mm});
            skLineSegment(sketch, "E112.top", {"start": v(0, -330) * mm, "end": v(40, -330) * mm});
            skLineSegment(sketch, "E112.left", {"start": v(0, 0) * mm, "end": v(0, -330) * mm});
            skLineSegment(sketch, "E112.right", {"start": v(40, 0) * mm, "end": v(40, -330) * mm});
            skSolve(sketch);
        }
        {
            var Q0;
            Q0 = qSketchRegion(id + "F31", true);
            extrude(context, id + "F32", {"entities" : qUnion([Q0]), "depth" : 2 * mm, "offsetDistance" : 25 * mm});
        }
        {
            var Q0;
            Q0=makeQuery(id+"F1.opExtrude","CAP_FACE",FACE,{"disambiguationData":[OSD([sQuery(id+"F0.wireOp",EDGE,"E1.bottom"),sQuery(id+"F0.wireOp",EDGE,"E1.top"),sQuery(id+"F0.wireOp",EDGE,"E1.left"),sQuery(id+"F0.wireOp",EDGE,"E1.right")])],"isStart":false});
            var sketch = newSketch(context, id + "F33", { "sketchPlane" : qUnion([Q0])});
            skPoint(sketch, "E113.0", {"position": v(255, -120.7) * mm});
            skPoint(sketch, "E114.0", {"position": v(255.7, -120) * mm});
            skLineSegment(sketch, "E115.bottom", {"start": v(255.7, -123) * mm, "end": v(3884.3, -123) * mm});
            skLineSegment(sketch, "E115.top", {"start": v(255.7, -243) * mm, "end": v(3884.3, -243) * mm});
            skLineSegment(sketch, "E115.left", {"start": v(3884.3, -123) * mm, "end": v(3884.3, -243) * mm});
            skLineSegment(sketch, "E115.right", {"start": v(255.7, -123) * mm, "end": v(255.7, -243) * mm});
            skPoint(sketch, "E116.0", {"position": v(3885, -120.7) * mm});
            skSolve(sketch);
        }
        {
            var Q0;
            Q0 = qSketchRegion(id + "F33", true);
            extrude(context, id + "F34", {"entities" : qUnion([Q0]), "depth" : 28 * mm, "offsetDistance" : 25 * mm});
        }
        {
            var Q0;
            Q0=makeQuery(id+"F5.opExtrude","CAP_EDGE",EDGE,{"disambiguationData":[OSD([sQuery(id+"F4.wireOp",EDGE,"E13.bottom")])],"isStart":false});
            var Q1;
            Q1=makeQuery(id+"F5.opExtrude","CAP_EDGE",EDGE,{"disambiguationData":[OSD([sQuery(id+"F4.wireOp",EDGE,"E15.trimOffspring")])],"isStart":false});
            fillet(context, id + "F35", {"entities" : qUnion([Q0, Q1]), "radius" : 3 * mm, "tangentPropagation" : true, "allowEdgeOverflow" : false});
        }
        {
            var Q0;
            Q0=makeQuery(id+"F5.opExtrude","CAP_EDGE",EDGE,{"disambiguationData":[OSD([sQuery(id+"F4.wireOp",EDGE,"E17.left")])],"isStart":false});
            var Q1;
            Q1=makeQuery(id+"F5.opExtrude","CAP_EDGE",EDGE,{"disambiguationData":[OSD([sQuery(id+"F4.wireOp",EDGE,"E17.right")])],"isStart":false});
            fillet(context, id + "F36", {"entities" : qUnion([Q0, Q1]), "radius" : 3 * mm, "tangentPropagation" : true, "allowEdgeOverflow" : false});
        }
        {
            var Q0;
            Q0=makeQuery(id+"F5.opExtrude","CAP_EDGE",EDGE,{"disambiguationData":[OSD([sQuery(id+"F4.wireOp",EDGE,"E25.left")])],"isStart":false});
            var Q1;
            Q1=makeQuery(id+"F5.opExtrude","CAP_EDGE",EDGE,{"disambiguationData":[OSD([sQuery(id+"F4.wireOp",EDGE,"E25.right")])],"isStart":false});
            fillet(context, id + "F37", {"entities" : qUnion([Q0, Q1]), "radius" : 3 * mm, "tangentPropagation" : true, "allowEdgeOverflow" : false});
        }
        {
            var Q0;
            Q0=makeQuery(id+"F5.opExtrude","CAP_EDGE",EDGE,{"disambiguationData":[OSD([sQuery(id+"F4.wireOp",EDGE,"E21.top")])],"isStart":false});
            var Q1;
            Q1=makeQuery(id+"F5.opExtrude","CAP_EDGE",EDGE,{"disambiguationData":[OSD([sQuery(id+"F4.wireOp",EDGE,"E21.bottom")])],"isStart":false});
            fillet(context, id + "F38", {"entities" : qUnion([Q0, Q1]), "radius" : 3 * mm, "tangentPropagation" : true, "allowEdgeOverflow" : false});
        }
        {
            var Q0;
            Q0=makeQuery(id+"F34.opExtrude","CAP_EDGE",EDGE,{"disambiguationData":[OSD([sQuery(id+"F33.wireOp",EDGE,"E115.top")])],"isStart":false});
            var Q1;
            Q1=makeQuery(id+"F34.opExtrude","CAP_EDGE",EDGE,{"disambiguationData":[OSD([sQuery(id+"F33.wireOp",EDGE,"E115.bottom")])],"isStart":false});
            fillet(context, id + "F39", {"entities" : qUnion([Q0, Q1]), "radius" : 3 * mm, "tangentPropagation" : true, "allowEdgeOverflow" : false});
        }
        {
            var Q0;
            Q0=makeQuery(id+"F9.opExtrude","SWEPT_FACE",FACE,{"disambiguationData":[OSD([sQuery(id+"F8.wireOp",EDGE,"E84.right")])]});
            var sketch = newSketch(context, id + "F40", { "sketchPlane" : qUnion([Q0])});
            skPoint(sketch, "E117.0", {"position": v(2737, 850.36) * mm});
            skPoint(sketch, "E118.0", {"position": v(2759, 755.36) * mm});
            skLineSegment(sketch, "E119.bottom", {"start": v(2737, 850.36) * mm, "end": v(2759, 850.36) * mm});
            skLineSegment(sketch, "E119.top", {"start": v(2737, 755.36) * mm, "end": v(2759, 755.36) * mm});
            skLineSegment(sketch, "E119.left", {"start": v(2737, 850.36) * mm, "end": v(2737, 755.36) * mm});
            skLineSegment(sketch, "E119.right", {"start": v(2759, 850.36) * mm, "end": v(2759, 755.36) * mm});
            skSolve(sketch);
        }
        {
            var Q0;
            Q0 = qSketchRegion(id + "F40", true);
            extrude(context, id + "F41", {"entities" : qUnion([Q0]), "depth" : (2050 + 324) * mm, "offsetDistance" : 25 * mm, "hasSecondDirection" : true, "secondDirectionOppositeDirection" : true, "secondDirectionDepth" : 45 * mm});
        }
        {
            var Q0;
            Q0=makeQuery(id+"F25.opExtrude","CAP_FACE",FACE,{"disambiguationData":[OSD([sQuery(id+"F24.wireOp",EDGE,"E105"),sQuery(id+"F24.wireOp",EDGE,"E106"),sQuery(id+"F24.wireOp",EDGE,"E107"),sQuery(id+"F24.wireOp",EDGE,"E108")])],"isStart":true});
            var sketch = newSketch(context, id + "F42", { "sketchPlane" : qUnion([Q0])});
            skSolve(sketch);
        }
        {
            var Q0;
            Q0=makeQuery(id+"F42.imprint","IMPRINT",FACE,{"disambiguationData":[TD([[makeQuery(id+"F42.imprint","IMPRINT",EDGE,{"derivedFrom":makeQuery(id+"F25.opExtrude","CAP_EDGE",EDGE,{"disambiguationData":[OSD([sQuery(id+"F24.wireOp",EDGE,"E105")])],"isStart":true})}),1.0]])]});
            extrude(context, id + "F43", {"entities" : qUnion([Q0]), "depth" : 2154 * mm, "offsetDistance" : 25 * mm});
        }
        {
            var Q0;
            Q0=makeQuery(id+"F43.opExtrude","CAP_FACE",FACE,{"disambiguationData":[OSD([sQuery(id+"F24.wireOp",EDGE,"E105"),sQuery(id+"F24.wireOp",EDGE,"E106"),sQuery(id+"F24.wireOp",EDGE,"E107"),sQuery(id+"F24.wireOp",EDGE,"E108")])],"isStart":false});
            var sketch = newSketch(context, id + "F44", { "sketchPlane" : qUnion([Q0])});
            skSolve(sketch);
        }
        {
            var Q0;
            Q0=makeQuery(id+"F44.imprint","IMPRINT",FACE,{"disambiguationData":[TD([[makeQuery(id+"F44.imprint","IMPRINT",EDGE,{"derivedFrom":makeQuery(id+"F43.opExtrude","CAP_EDGE",EDGE,{"disambiguationData":[OSD([sQuery(id+"F24.wireOp",EDGE,"E105")])],"isStart":false})}),1.0]])]});
            extrude(context, id + "F45", {"entities" : qUnion([Q0]), "depth" : (2414 + 45) * mm, "offsetDistance" : 25 * mm});
        }
        {
            var Q0;
            Q0=makeQuery(id+"F9.opExtrude","SWEPT_FACE",FACE,{"disambiguationData":[OSD([sQuery(id+"F8.wireOp",EDGE,"E84.bottom")])]});
            var sketch = newSketch(context, id + "F46", { "sketchPlane" : qUnion([Q0])});
            skLineSegment(sketch, "E120.0", {"start": v(1950, 0) * mm, "end": v(1950, 877.19) * mm});
            skLineSegment(sketch, "E121.0", {"start": v(-424, 850.36) * mm, "end": v(1995, 850.36) * mm});
            skLineSegment(sketch, "E122.0", {"start": v(-424, 755.36) * mm, "end": v(1995, 755.36) * mm});
            skLineSegment(sketch, "E123.bottom", {"start": v(1950, 850.36) * mm, "end": v(1928, 850.36) * mm});
            skLineSegment(sketch, "E123.top", {"start": v(1950, 755.36) * mm, "end": v(1928, 755.36) * mm});
            skLineSegment(sketch, "E123.left", {"start": v(1950, 850.36) * mm, "end": v(1950, 755.36) * mm});
            skLineSegment(sketch, "E123.right", {"start": v(1928, 850.36) * mm, "end": v(1928, 755.36) * mm});
            skSolve(sketch);
        }
        {
            var Q0;
            Q0 = qSketchRegion(id + "F46", true);
            extrude(context, id + "F47", {"entities" : qUnion([Q0]), "oppositeDirection" : true, "depth" : (773 + 43) * mm, "offsetDistance" : 25 * mm, "hasSecondDirection" : true, "secondDirectionOppositeDirection" : true, "secondDirectionDepth" : 22 * mm});
        }
        {
            var Q0;
            Q0=qCreatedBy(makeId("Top.planeOp"),FACE);
            var sketch = newSketch(context, id + "F48", { "sketchPlane" : qUnion([Q0])});
            skPoint(sketch, "E124.0", {"position": v(-2615.5, -2802.05) * mm});
            skLineSegment(sketch, "E125.bottom", {"start": v(-2615.5, -2802.05) * mm, "end": v(-2315.5, -2802.05) * mm});
            skLineSegment(sketch, "E125.top", {"start": v(-2615.5, -2502.05) * mm, "end": v(-2315.5, -2502.05) * mm});
            skLineSegment(sketch, "E125.left", {"start": v(-2615.5, -2802.05) * mm, "end": v(-2615.5, -2502.05) * mm});
            skLineSegment(sketch, "E125.right", {"start": v(-2315.5, -2802.05) * mm, "end": v(-2315.5, -2502.05) * mm});
            skLineSegment(sketch, "E126", {"start": v(-2615.5, -2802.05) * mm, "end": v(-2315.5, -2502.05) * mm});
            skSolve(sketch);
        }
        {
            var Q0;
            Q0=makeQuery(id+"F48.imprint","IMPRINT",FACE,{"disambiguationData":[TD([[makeQuery(id+"F48.imprint","IMPRINT",EDGE,{"derivedFrom":sQuery(id+"F48.wireOp",EDGE,"E125.top")}),-1.0]])]});
            extrude(context, id + "F49", {"entities" : qUnion([Q0]), "operationType" : NewBodyOperationType.REMOVE, "depth" : 999 * mm, "offsetDistance" : 25 * mm});
        }
        {
            var Q0;
            Q0=makeQuery(id+"F3.boolean.opBoolean","MERGE",FACE,{"derivedFrom":[makeQuery(id+"F1.opExtrude","SWEPT_FACE",FACE,{"disambiguationData":[OSD([sQuery(id+"F0.wireOp",EDGE,"E1.left")])]}),makeQuery(id+"F3.opExtrude","SWEPT_FACE",FACE,{"disambiguationData":[OSD([sQuery(id+"F2.wireOp",EDGE,"qP2xH3ZB-ntGN-hCC5-hPO3-ei0ztwaUkLOt.left")])]})]});
            var sketch = newSketch(context, id + "F50", { "sketchPlane" : qUnion([Q0])});
            skLineSegment(sketch, "E127.0", {"start": v(2782, 94) * mm, "end": v(2782, 0) * mm});
            skLineSegment(sketch, "E128.bottom", {"start": v(2782, 94) * mm, "end": v(2810, 94) * mm});
            skLineSegment(sketch, "E128.top", {"start": v(2782, -26) * mm, "end": v(2810, -26) * mm});
            skLineSegment(sketch, "E128.left", {"start": v(2782, 94) * mm, "end": v(2782, -26) * mm});
            skLineSegment(sketch, "E128.right", {"start": v(2810, 94) * mm, "end": v(2810, -26) * mm});
            skSolve(sketch);
        }
        {
            var Q0;
            {var subQ4=sQuery(id+"F50.wireOp",EDGE,"E128.bottom");Q0=makeQuery(id+"F50.imprint","IMPRINT",FACE,{"disambiguationData":[TD([[makeQuery(id+"F50.imprint","IMPRINT",EDGE,{"derivedFrom":subQ4}),-1.0]])]});}
            extrude(context, id + "F51", {"entities" : qUnion([Q0]), "oppositeDirection" : true, "depth" : (3740 + 140) * mm, "offsetDistance" : 25 * mm});
        }
        {
            var Q0;
            Q0=makeQuery(id+"F51.opExtrude","SWEPT_EDGE",EDGE,{"disambiguationData":[OSD([sQuery(id+"F50.wireOp",EDGE,"E128.bottom"),sQuery(id+"F50.wireOp",EDGE,"E128.right")])]});
            var Q1;
            Q1=makeQuery(id+"F51.opExtrude","SWEPT_EDGE",EDGE,{"disambiguationData":[OSD([sQuery(id+"F50.wireOp",EDGE,"E128.top"),sQuery(id+"F50.wireOp",EDGE,"E128.right")])]});
            fillet(context, id + "F52", {"entities" : qUnion([Q0, Q1]), "radius" : 3 * mm, "tangentPropagation" : true, "allowEdgeOverflow" : false});
        }
        {
            var Q0;
            Q0=makeQuery(id+"F3.opExtrude","CAP_FACE",FACE,{"disambiguationData":[OSD([sQuery(id+"F2.wireOp",EDGE,"E8.top"),sQuery(id+"F2.wireOp",EDGE,"E8.left"),sQuery(id+"F2.wireOp",EDGE,"E8.right"),sQuery(id+"F2.wireOp",EDGE,"E10.0")])],"isStart":false});
            var sketch = newSketch(context, id + "F53", { "sketchPlane" : qUnion([Q0])});
            skPoint(sketch, "E129.0", {"position": v(378.7, -243) * mm});
            skPoint(sketch, "E130.0", {"position": v(378, -243.7) * mm});
            skLineSegment(sketch, "E131.bottom", {"start": v(378.7, -246) * mm, "end": v(3761.3, -246) * mm});
            skLineSegment(sketch, "E131.top", {"start": v(378.7, -366) * mm, "end": v(3761.3, -366) * mm});
            skLineSegment(sketch, "E131.left", {"start": v(378.7, -246) * mm, "end": v(378.7, -366) * mm});
            skLineSegment(sketch, "E131.right", {"start": v(3761.3, -246) * mm, "end": v(3761.3, -366) * mm});
            skPoint(sketch, "E132.0", {"position": v(3762, -243.7) * mm});
            skPoint(sketch, "E133.0", {"position": v(3761.3, -243) * mm});
            skSolve(sketch);
        }
        {
            var Q0;
            Q0 = qSketchRegion(id + "F53", true);
            extrude(context, id + "F54", {"entities" : qUnion([Q0]), "depth" : 28 * mm, "offsetDistance" : 25 * mm});
        }
        {
            var Q0;
            Q0=makeQuery(id+"F54.opExtrude","CAP_EDGE",EDGE,{"disambiguationData":[OSD([sQuery(id+"F53.wireOp",EDGE,"E131.top")])],"isStart":false});
            var Q1;
            Q1=makeQuery(id+"F54.opExtrude","CAP_EDGE",EDGE,{"disambiguationData":[OSD([sQuery(id+"F53.wireOp",EDGE,"E131.bottom")])],"isStart":false});
            fillet(context, id + "F55", {"entities" : qUnion([Q0, Q1]), "radius" : 3 * mm, "tangentPropagation" : true, "allowEdgeOverflow" : false});
        }
    });
